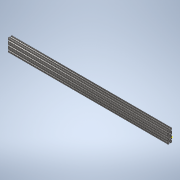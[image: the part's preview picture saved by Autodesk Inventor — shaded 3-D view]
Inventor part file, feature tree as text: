
AUTODESK INVENTOR PART (.ipt)
format: ipt  version: 2020 (Build 240168000, 168)  size: 399,872 bytes
history: native  units: in
note: dims shown in document units (in); Inventor stores cm internally (conversion verified against a paired STEP export)
features: sketch x2, extrude x1
ambient origin geometry x8: Origin, YZ Plane, XZ Plane, XY Plane, X Axis, Y Axis, Z Axis, Center Point
bodies: Solid1 (feature_tree)
feature tree (3):
  extrude  "Extrusion1"  [1 undecoded]
  sketch  "Sketch2"
  sketch  "Sketch1"  dims[d0=38.0in d1=0.0in]
note: 1 required parameter value undecoded (feature->parameter linkage not recoverable at this tier; creation-order binding heuristic only, values carry confidence <= 0.55)
